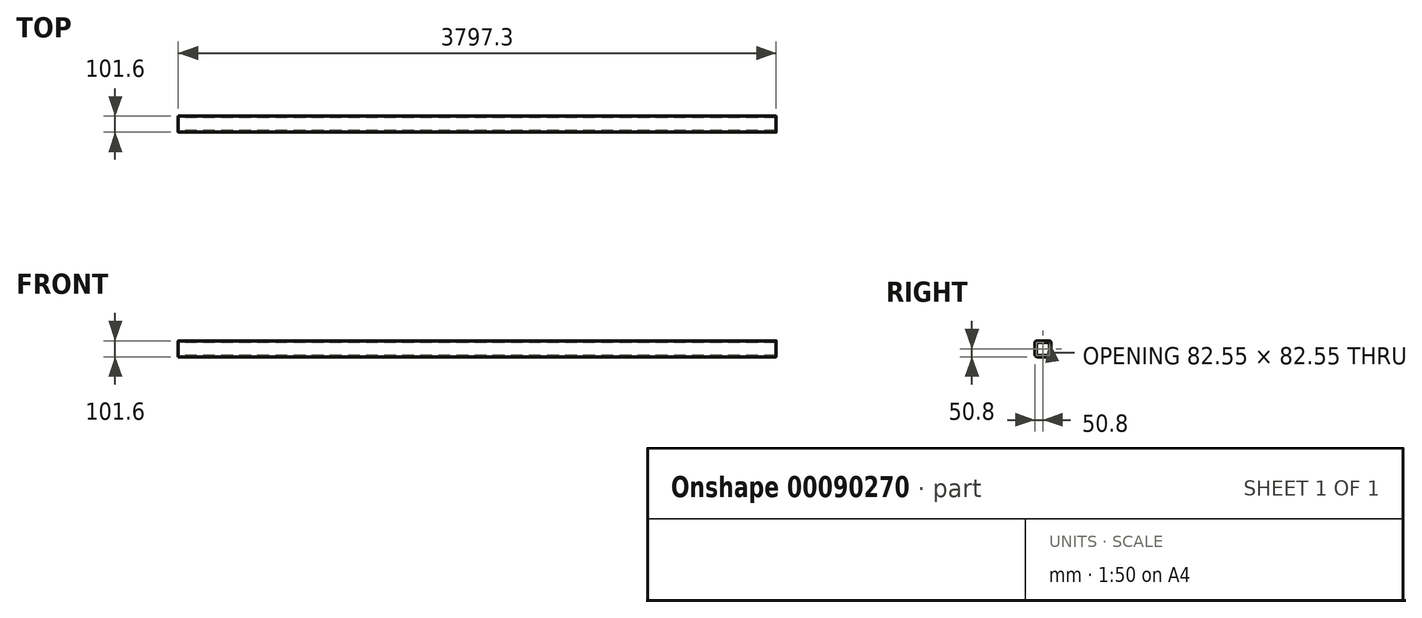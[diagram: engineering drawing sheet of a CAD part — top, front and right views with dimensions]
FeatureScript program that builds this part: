
annotation { "Feature Type Name" : "Feature", "Feature Type Description" : "" }
export const myFeature = defineFeature(function(context is Context, id is Id, definition is map)
    precondition{}
    {
        {
            var Q0;
            Q0=qCreatedBy(makeId("Right.planeOp"),FACE);
            var sketch = newSketch(context, id + "F0", { "sketchPlane" : qUnion([Q0])});
            skLineSegment(sketch, "E0.bottom", {"start": v(12.7, 0) * mm, "end": v(88.9, 0) * mm});
            skLineSegment(sketch, "E0.top", {"start": v(12.7, -101.6) * mm, "end": v(88.9, -101.6) * mm});
            skLineSegment(sketch, "E0.left", {"start": v(0, -12.7) * mm, "end": v(0, -88.9) * mm});
            skLineSegment(sketch, "E0.right", {"start": v(101.6, -12.7) * mm, "end": v(101.6, -88.9) * mm});
            skLineSegment(sketch, "E1.0", {"start": v(15.88, -9.53) * mm, "end": v(85.73, -9.53) * mm});
            skLineSegment(sketch, "E1.1", {"start": v(9.53, -15.88) * mm, "end": v(9.53, -85.73) * mm});
            skLineSegment(sketch, "E1.2", {"start": v(15.88, -92.08) * mm, "end": v(85.73, -92.08) * mm});
            skLineSegment(sketch, "E1.3", {"start": v(92.08, -15.88) * mm, "end": v(92.08, -85.73) * mm});
            skPoint(sketch, "E2.visualSharp", {"position": v(0, 0) * mm});
            skArc(sketch, "E2.filletArc", {"start": v(12.7, 0) * mm, "mid": v(3.72, -3.72) * mm, "end": v(0, -12.7) * mm});
            skPoint(sketch, "E3.visualSharp", {"position": v(101.6, 0) * mm});
            skArc(sketch, "E3.filletArc", {"start": v(101.6, -12.7) * mm, "mid": v(97.88, -3.72) * mm, "end": v(88.9, 0) * mm});
            skPoint(sketch, "E4.visualSharp", {"position": v(101.6, -101.6) * mm});
            skArc(sketch, "E4.filletArc", {"start": v(88.9, -101.6) * mm, "mid": v(97.88, -97.88) * mm, "end": v(101.6, -88.9) * mm});
            skPoint(sketch, "E5.visualSharp", {"position": v(0, -101.6) * mm});
            skArc(sketch, "E5.filletArc", {"start": v(0, -88.9) * mm, "mid": v(3.72, -97.88) * mm, "end": v(12.7, -101.6) * mm});
            skPoint(sketch, "E6.visualSharp", {"position": v(9.53, -92.08) * mm});
            skArc(sketch, "E6.filletArc", {"start": v(9.53, -85.73) * mm, "mid": v(11.38, -90.22) * mm, "end": v(15.88, -92.08) * mm});
            skPoint(sketch, "E7.visualSharp", {"position": v(92.08, -92.08) * mm});
            skArc(sketch, "E7.filletArc", {"start": v(85.73, -92.08) * mm, "mid": v(90.22, -90.22) * mm, "end": v(92.08, -85.73) * mm});
            skPoint(sketch, "E8.visualSharp", {"position": v(92.08, -9.53) * mm});
            skArc(sketch, "E8.filletArc", {"start": v(92.08, -15.88) * mm, "mid": v(90.22, -11.38) * mm, "end": v(85.73, -9.52) * mm});
            skPoint(sketch, "E9.visualSharp", {"position": v(9.53, -9.53) * mm});
            skArc(sketch, "E9.filletArc", {"start": v(15.88, -9.53) * mm, "mid": v(11.38, -11.38) * mm, "end": v(9.53, -15.88) * mm});
            skSolve(sketch);
        }
        {
            var Q0;
            Q0=makeQuery(id+"F0.imprint","IMPRINT",FACE,{"disambiguationData":[TD([[makeQuery(id+"F0.imprint","IMPRINT",EDGE,{"derivedFrom":sQuery(id+"F0.wireOp",EDGE,"E0.bottom")}),-1.0]])]});
            extrude(context, id + "F1", {"entities" : qUnion([Q0]), "depth" : 3797.3 * mm});
        }
    });
